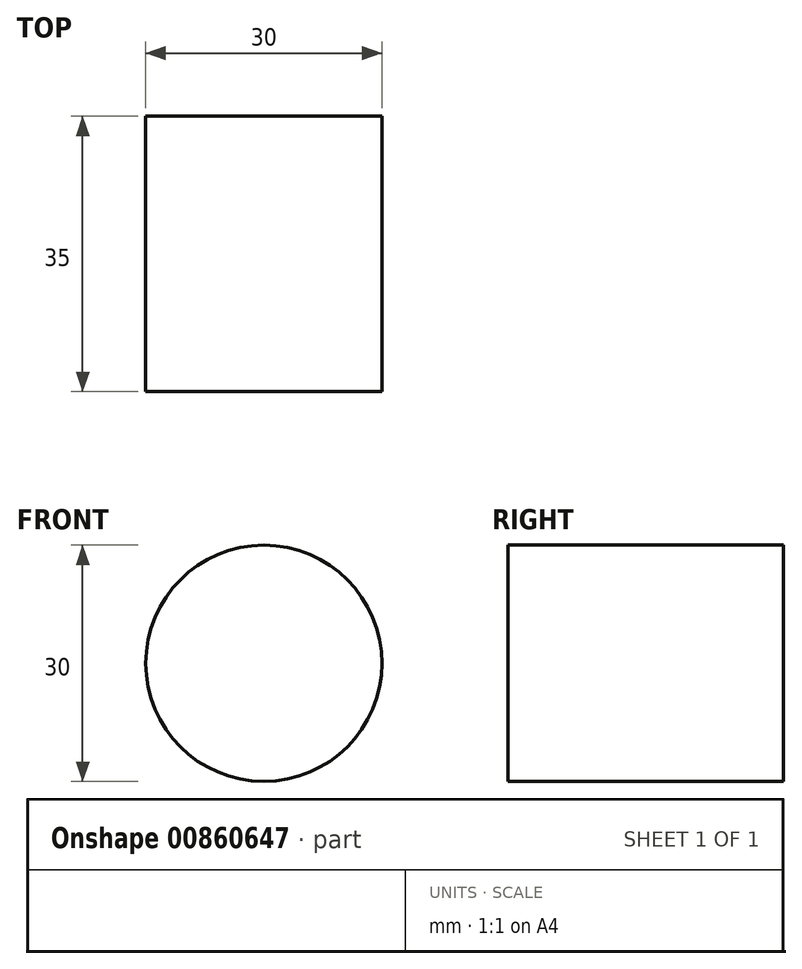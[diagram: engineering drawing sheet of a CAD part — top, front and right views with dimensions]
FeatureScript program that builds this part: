
annotation { "Feature Type Name" : "Feature", "Feature Type Description" : "" }
export const myFeature = defineFeature(function(context is Context, id is Id, definition is map)
    precondition{}
    {
        {
            var Q0;
            Q0=qCreatedBy(makeId("Front.planeOp"),FACE);
            var sketch = newSketch(context, id + "F0", { "sketchPlane" : qUnion([Q0])});
            skCircle(sketch, "E0", {"center": v(0, 0) * mm, "radius": 15 * mm});
            skSolve(sketch);
        }
        {
            var Q0;
            Q0=makeQuery(id+"F0.imprint","IMPRINT",FACE,{"disambiguationData":[TD([[makeQuery(id+"F0.imprint","IMPRINT",EDGE,{"derivedFrom":sQuery(id+"F0.wireOp",EDGE,"E0")}),1.0]])]});
            var Q1;
            Q1=sQuery(id+"F0.wireOp",EDGE,"E0");
            extrude(context, id + "F1", {"entities" : qUnion([Q0]), "surfaceEntities" : qUnion([Q1]), "depth" : 35 * mm, "offsetDistance" : 25.4 * mm});
        }
    });
